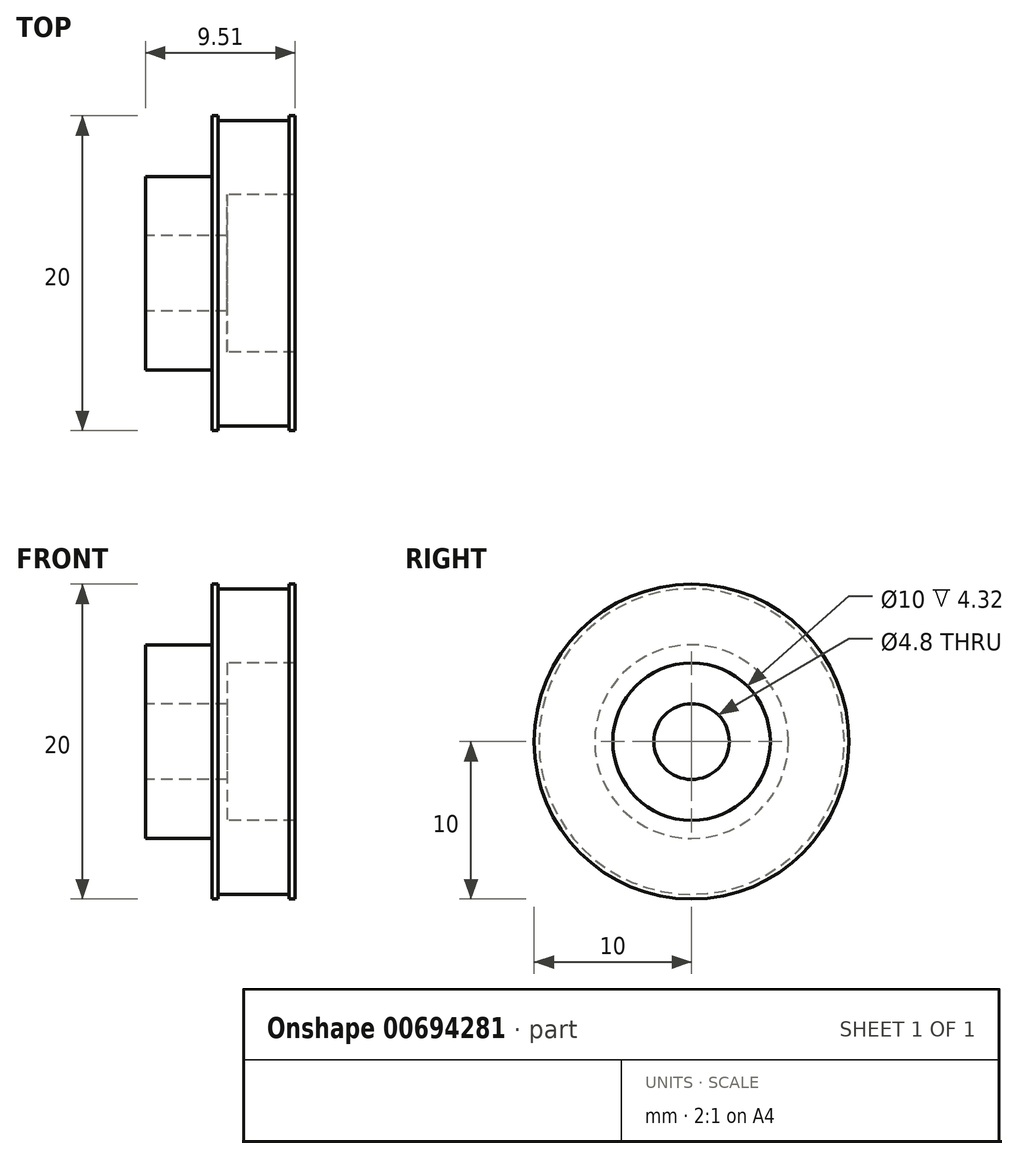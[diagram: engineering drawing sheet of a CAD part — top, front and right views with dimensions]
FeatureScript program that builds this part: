
annotation { "Feature Type Name" : "Feature", "Feature Type Description" : "" }
export const myFeature = defineFeature(function(context is Context, id is Id, definition is map)
    precondition{}
    {
        {
            var Q0;
            Q0=qCreatedBy(makeId("Front.planeOp"),FACE);
            var sketch = newSketch(context, id + "F0", { "sketchPlane" : qUnion([Q0])});
            skLineSegment(sketch, "E0", {"start": v(0, 0) * mm, "end": v(11.95, 0) * mm, "construction": true});
            skLineSegment(sketch, "E1", {"start": v(0, 2.4) * mm, "end": v(5.2, 2.4) * mm});
            skLineSegment(sketch, "E2", {"start": v(9.51, 5) * mm, "end": v(9.51, 10) * mm});
            skLineSegment(sketch, "E3", {"start": v(9.51, 10) * mm, "end": v(9.12, 10) * mm});
            skLineSegment(sketch, "E4", {"start": v(4.23, 10) * mm, "end": v(4.23, 6.15) * mm});
            skLineSegment(sketch, "E5", {"start": v(4.23, 6.15) * mm, "end": v(0, 6.15) * mm});
            skLineSegment(sketch, "E6", {"start": v(0, 6.15) * mm, "end": v(0, 2.4) * mm});
            skLineSegment(sketch, "E7", {"start": v(9.51, 5) * mm, "end": v(5.2, 5) * mm});
            skLineSegment(sketch, "E8", {"start": v(5.2, 5) * mm, "end": v(5.2, 2.4) * mm});
            skLineSegment(sketch, "E9", {"start": v(4.62, 10) * mm, "end": v(4.62, 9.7) * mm});
            skLineSegment(sketch, "E10", {"start": v(4.62, 9.7) * mm, "end": v(9.12, 9.7) * mm});
            skLineSegment(sketch, "E11", {"start": v(9.12, 9.7) * mm, "end": v(9.12, 10) * mm});
            skLineSegment(sketch, "E12.trimOffspring", {"start": v(4.62, 10) * mm, "end": v(4.23, 10) * mm});
            skSolve(sketch);
        }
        {
            var Q0;
            Q0=qSketchRegion(id+"F0",true);
            var Q1;
            Q1=sQuery(id+"F0.wireOp",EDGE,"E0");
            revolve(context, id + "F1", {"entities" : qUnion([Q0]), "axis" : qUnion([Q1]), "revolveType" : RevolveType.FULL});
        }
    });
